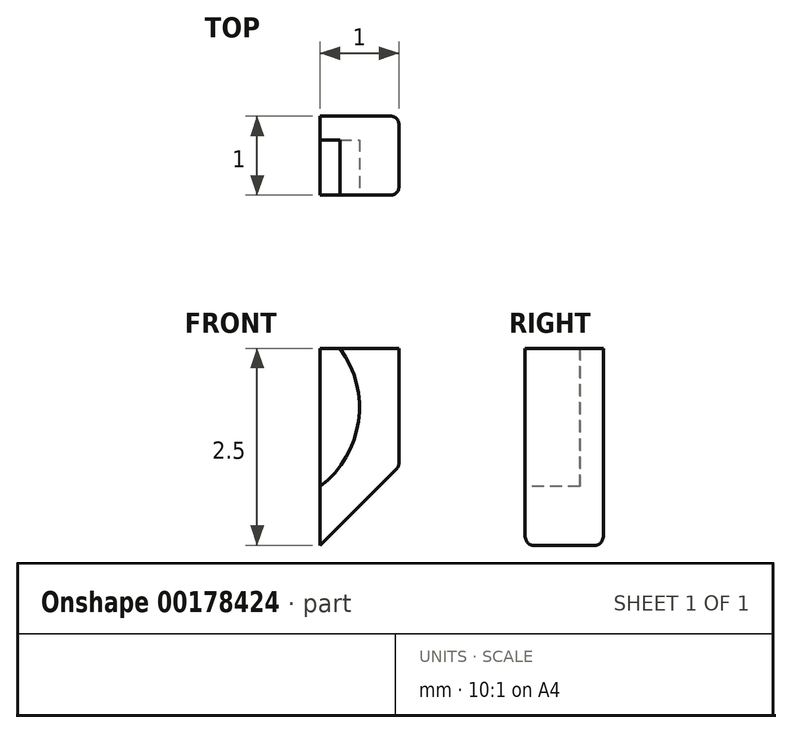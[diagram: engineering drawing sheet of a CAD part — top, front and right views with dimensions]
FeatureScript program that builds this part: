
annotation { "Feature Type Name" : "Feature", "Feature Type Description" : "" }
export const myFeature = defineFeature(function(context is Context, id is Id, definition is map)
    precondition{}
    {
        {
            var Q0;
            Q0=qCreatedBy(makeId("Front.planeOp"),FACE);
            var sketch = newSketch(context, id + "F0", { "sketchPlane" : qUnion([Q0])});
            skLineSegment(sketch, "E0.left", {"start": v(0.75, 0.75) * mm, "end": v(0.75, -1.75) * mm});
            skPoint(sketch, "E0.middle", {"position": v(0, 0) * mm});
            skLineSegment(sketch, "E1.bottom", {"start": v(1.75, 0.75) * mm, "end": v(0.75, 0.75) * mm});
            skLineSegment(sketch, "E1.left", {"start": v(1.75, 0.75) * mm, "end": v(1.75, -0.75) * mm});
            skArc(sketch, "E2", {"start": v(0.75, -1) * mm, "mid": v(1.24, -0.18) * mm, "end": v(1, 0.75) * mm});
            skLineSegment(sketch, "E3", {"start": v(0.75, -1.75) * mm, "end": v(1.75, -0.75) * mm});
            skPoint(sketch, "E0.bottom.start.orphan", {"position": v(0.75, 1.75) * mm});
            skPoint(sketch, "E1.right.start.orphan", {"position": v(-1.75, 0.75) * mm});
            skPoint(sketch, "E4.orphan", {"position": v(-1.75, -0.75) * mm});
            skPoint(sketch, "E5.orphan", {"position": v(-0.75, -1.75) * mm});
            skPoint(sketch, "E0.right.start.orphan", {"position": v(-0.75, 1.75) * mm});
            skSolve(sketch);
        }
        {
            var Q0;
            {var subQ3=sQuery(id+"F0.wireOp",EDGE,"E2");Q0=makeQuery(id+"F0.imprint","IMPRINT",FACE,{"disambiguationData":[TD([[makeQuery(id+"F0.imprint","IMPRINT",EDGE,{"derivedFrom":subQ3}),1.0]])]});}
            var Q1;
            {var subQ1=sQuery(id+"F0.wireOp",EDGE,"E1.left");Q1=makeQuery(id+"F0.imprint","IMPRINT",FACE,{"disambiguationData":[TD([[makeQuery(id+"F0.imprint","IMPRINT",EDGE,{"derivedFrom":subQ1}),-1.0]])]});}
            extrude(context, id + "F1", {"entities" : qUnion([Q0, Q1]), "depth" : 1 * mm});
        }
        {
            var Q0;
            Q0=makeQuery(id+"F1.opExtrude","CAP_FACE",FACE,{"disambiguationData":[OSD([sQuery(id+"F0.wireOp",EDGE,"E0.left"),sQuery(id+"F0.wireOp",EDGE,"E1.bottom"),sQuery(id+"F0.wireOp",EDGE,"E1.left"),sQuery(id+"F0.wireOp",EDGE,"E3")])],"isStart":false});
            var sketch = newSketch(context, id + "F2", { "sketchPlane" : qUnion([Q0])});
            skCircle(sketch, "E6", {"center": v(0, 0) * mm, "radius": 1.25 * mm});
            skSolve(sketch);
        }
        {
            var Q0;
            {var subQ0=sQuery(id+"F2.wireOp",EDGE,"E6");var subQ1=makeQuery(id+"F1.opExtrude","CAP_EDGE",EDGE,{"disambiguationData":[OSD([sQuery(id+"F0.wireOp",EDGE,"E0.left")])],"isStart":false});var subQ2=makeQuery(id+"F2.imprint","INTERSECT",VERTEX,{"derivedFrom":[subQ1,subQ0]});Q0=makeQuery(id+"F2.imprint","IMPRINT",FACE,{"disambiguationData":[TD([[makeQuery(id+"F2.imprint","IMPRINT",EDGE,{"disambiguationData":[TD([[subQ2,1.0]])],"derivedFrom":subQ0}),1.0]])]});}
            var Q1;
            {var subQ0=sQuery(id+"F2.wireOp",EDGE,"E6");var subQ1=makeQuery(id+"F1.opExtrude","CAP_EDGE",EDGE,{"disambiguationData":[OSD([sQuery(id+"F0.wireOp",EDGE,"E0.left")])],"isStart":false});var subQ2=makeQuery(id+"F2.imprint","INTERSECT",VERTEX,{"derivedFrom":[subQ1,subQ0]});Q1=makeQuery(id+"F2.imprint","IMPRINT",FACE,{"disambiguationData":[TD([[makeQuery(id+"F2.imprint","IMPRINT",EDGE,{"disambiguationData":[TD([[subQ2,-1.0]])],"derivedFrom":subQ0}),1.0]])]});}
            extrude(context, id + "F3", {"entities" : qUnion([Q0, Q1]), "operationType" : NewBodyOperationType.REMOVE, "oppositeDirection" : true, "depth" : 0.7 * mm});
        }
        {
            var Q0;
            Q0=makeQuery(id+"F1.opExtrude","CAP_EDGE",EDGE,{"disambiguationData":[OSD([sQuery(id+"F0.wireOp",EDGE,"E1.left")])],"isStart":false});
            var Q1;
            Q1=makeQuery(id+"F3.boolean.opBoolean","COPY",EDGE,{"derivedFrom":makeQuery(id+"F3.opExtrude","CAP_EDGE",EDGE,{"disambiguationData":[OSD([sQuery(id+"F2.wireOp",EDGE,"E6")])],"isStart":true})});
            var Q2;
            Q2=makeQuery(id+"F1.opExtrude","CAP_EDGE",EDGE,{"disambiguationData":[OSD([sQuery(id+"F0.wireOp",EDGE,"E1.left")])],"isStart":true});
            var Q3;
            Q3=makeQuery(id+"F1.opExtrude","SWEPT_EDGE",EDGE,{"disambiguationData":[OSD([sQuery(id+"F0.wireOp",EDGE,"E1.left"),sQuery(id+"F0.wireOp",EDGE,"E3")])]});
            var Q4;
            Q4=makeQuery(id+"F1.opExtrude","CAP_EDGE",EDGE,{"disambiguationData":[OSD([sQuery(id+"F0.wireOp",EDGE,"E3")])],"isStart":false});
            var Q5;
            Q5=makeQuery(id+"F1.opExtrude","CAP_EDGE",EDGE,{"disambiguationData":[OSD([sQuery(id+"F0.wireOp",EDGE,"E3")])],"isStart":true});
            fillet(context, id + "F4", {"entities" : qUnion([Q0, Q1, Q2, Q3, Q4, Q5]), "radius" : 0.1 * mm, "tangentPropagation" : true, "allowEdgeOverflow" : false});
        }
    });
